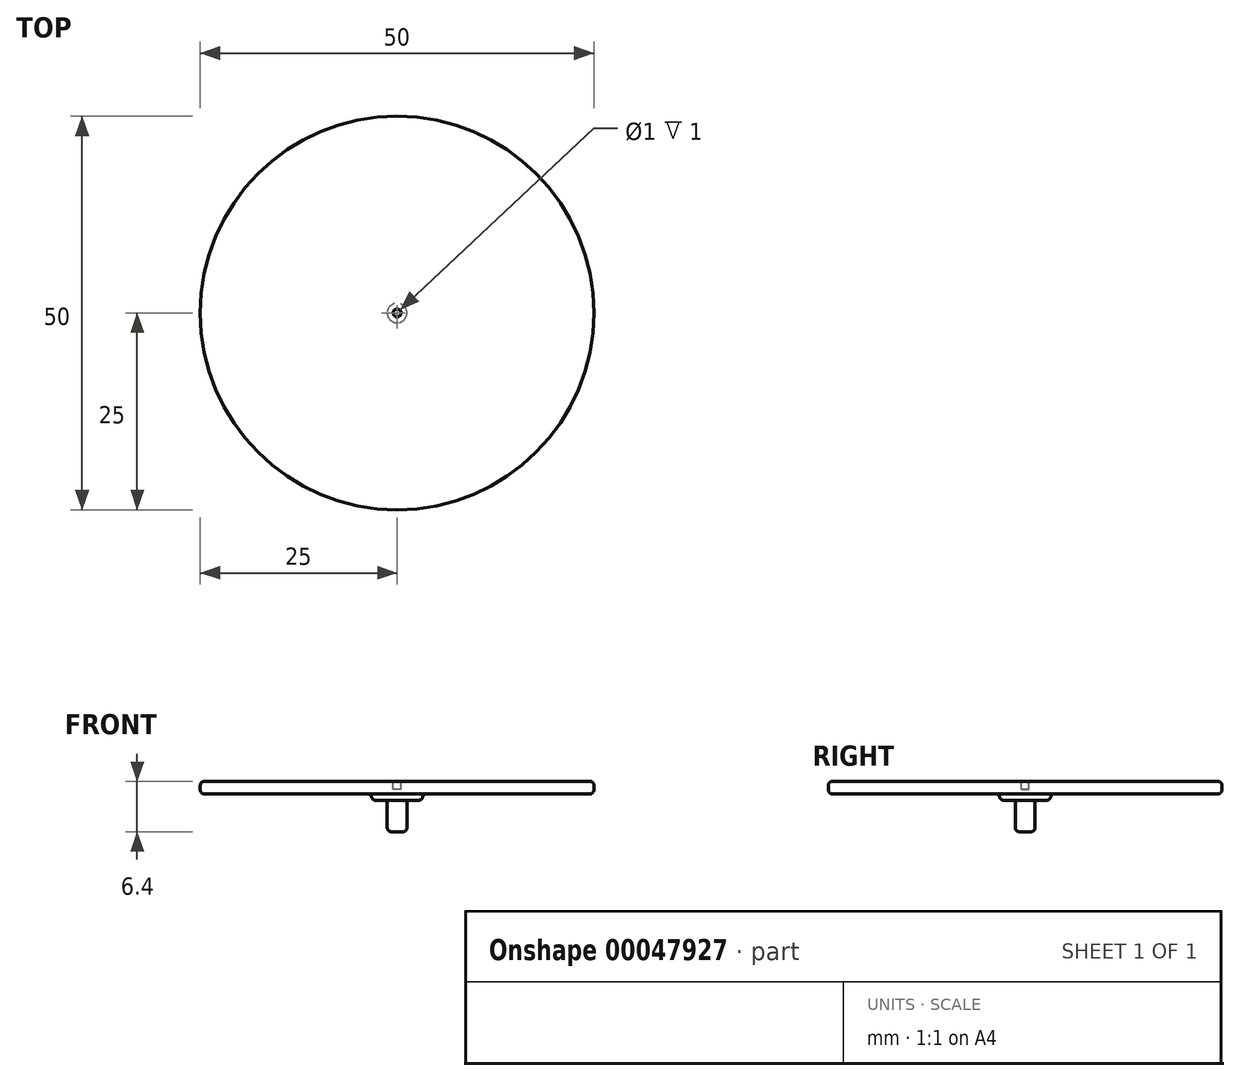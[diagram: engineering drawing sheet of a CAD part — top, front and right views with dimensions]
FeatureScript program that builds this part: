
annotation { "Feature Type Name" : "Feature", "Feature Type Description" : "" }
export const myFeature = defineFeature(function(context is Context, id is Id, definition is map)
    precondition{}
    {
        {
            var Q0;
            Q0=qCreatedBy(makeId("Front.planeOp"),FACE);
            var sketch = newSketch(context, id + "F0", { "sketchPlane" : qUnion([Q0])});
            skLineSegment(sketch, "E0", {"start": v(0, 0) * mm, "end": v(25, 0) * mm});
            skLineSegment(sketch, "E1", {"start": v(25, 0) * mm, "end": v(25, -1.6) * mm});
            skLineSegment(sketch, "E2", {"start": v(25, -1.6) * mm, "end": v(3.25, -1.6) * mm});
            skLineSegment(sketch, "E3", {"start": v(3.25, -1.6) * mm, "end": v(3.25, -2.4) * mm});
            skLineSegment(sketch, "E4", {"start": v(3.25, -2.4) * mm, "end": v(1.25, -2.4) * mm});
            skLineSegment(sketch, "E5", {"start": v(1.25, -2.4) * mm, "end": v(1.25, -6.4) * mm});
            skLineSegment(sketch, "E6", {"start": v(1.25, -6.4) * mm, "end": v(0, -6.4) * mm});
            skLineSegment(sketch, "E7", {"start": v(0, -6.4) * mm, "end": v(0, 0) * mm});
            skLineSegment(sketch, "E8", {"start": v(0, 11.61) * mm, "end": v(0, -10.73) * mm, "construction": true});
            skSolve(sketch);
        }
        {
            var Q0;
            Q0=makeQuery(id+"F0.imprint","IMPRINT",FACE,{"disambiguationData":[TD([[makeQuery(id+"F0.imprint","IMPRINT",EDGE,{"derivedFrom":sQuery(id+"F0.wireOp",EDGE,"E0")}),-1.0]])]});
            var Q1;
            Q1=sQuery(id+"F0.wireOp",EDGE,"E8");
            revolve(context, id + "F1", {"entities" : qUnion([Q0]), "axis" : qUnion([Q1]), "revolveType" : RevolveType.FULL});
        }
        {
            var Q0;
            Q0=makeQuery(id+"F1.opRevolve","SWEPT_EDGE",EDGE,{"disambiguationData":[OSD([sQuery(id+"F0.wireOp",EDGE,"E5"),sQuery(id+"F0.wireOp",EDGE,"E6")])]});
            fillet(context, id + "F2", {"entities" : qUnion([Q0]), "radius" : 0.5 * mm, "tangentPropagation" : true, "allowEdgeOverflow" : false});
        }
        {
            var Q0;
            Q0=makeQuery(id+"F1.opRevolve","SWEPT_EDGE",EDGE,{"disambiguationData":[OSD([sQuery(id+"F0.wireOp",EDGE,"E3"),sQuery(id+"F0.wireOp",EDGE,"E4")])]});
            fillet(context, id + "F3", {"entities" : qUnion([Q0]), "radius" : 0.5 * mm, "tangentPropagation" : true, "allowEdgeOverflow" : false});
        }
        {
            var Q0;
            Q0=makeQuery(id+"F1.opRevolve","SWEPT_EDGE",EDGE,{"disambiguationData":[OSD([sQuery(id+"F0.wireOp",EDGE,"E2"),sQuery(id+"F0.wireOp",EDGE,"E3")])]});
            fillet(context, id + "F4", {"entities" : qUnion([Q0]), "radius" : 0.5 * mm, "tangentPropagation" : true, "allowEdgeOverflow" : false});
        }
        {
            var Q0;
            Q0=makeQuery(id+"F1.opRevolve","SWEPT_EDGE",EDGE,{"disambiguationData":[OSD([sQuery(id+"F0.wireOp",EDGE,"E1"),sQuery(id+"F0.wireOp",EDGE,"E2")])]});
            fillet(context, id + "F5", {"entities" : qUnion([Q0]), "radius" : 0.5 * mm, "tangentPropagation" : true, "allowEdgeOverflow" : false});
        }
        {
            var Q0;
            Q0=makeQuery(id+"F1.opRevolve","SWEPT_EDGE",EDGE,{"disambiguationData":[OSD([sQuery(id+"F0.wireOp",EDGE,"E0"),sQuery(id+"F0.wireOp",EDGE,"E1")])]});
            fillet(context, id + "F6", {"entities" : qUnion([Q0]), "radius" : 0.5 * mm, "tangentPropagation" : true, "allowEdgeOverflow" : false});
        }
        {
            var Q0;
            Q0=makeQuery(id+"F1.opRevolve","SWEPT_FACE",FACE,{"disambiguationData":[OSD([sQuery(id+"F0.wireOp",EDGE,"E0")])]});
            var sketch = newSketch(context, id + "F7", { "sketchPlane" : qUnion([Q0])});
            skCircle(sketch, "E9", {"center": v(0, 0) * mm, "radius": 0.5 * mm});
            skSolve(sketch);
        }
        {
            var Q0;
            Q0=makeQuery(id+"F7.imprint","IMPRINT",FACE,{"disambiguationData":[TD([[makeQuery(id+"F7.imprint","IMPRINT",EDGE,{"derivedFrom":sQuery(id+"F7.wireOp",EDGE,"E9")}),1.0]])]});
            extrude(context, id + "F8", {"entities" : qUnion([Q0]), "operationType" : NewBodyOperationType.REMOVE, "oppositeDirection" : true, "depth" : 1 * mm});
        }
    });
